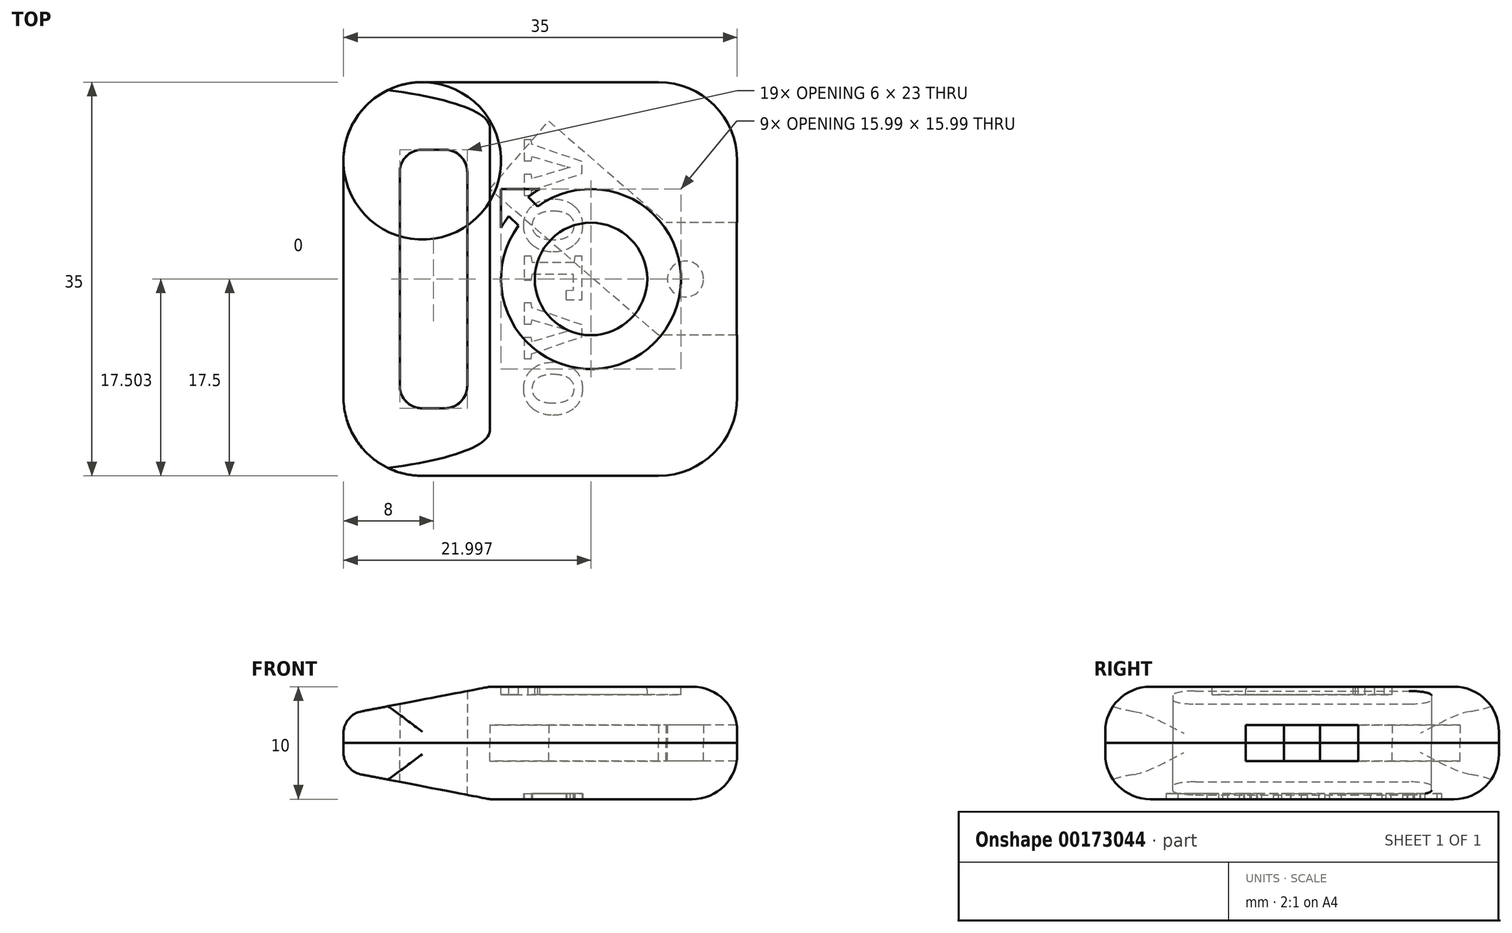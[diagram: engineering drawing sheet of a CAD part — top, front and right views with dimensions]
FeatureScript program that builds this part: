
annotation { "Feature Type Name" : "Feature", "Feature Type Description" : "" }
export const myFeature = defineFeature(function(context is Context, id is Id, definition is map)
    precondition{}
    {
        {
            var Q0;
            Q0=qCreatedBy(makeId("Top.planeOp"),FACE);
            var sketch = newSketch(context, id + "F0", { "sketchPlane" : qUnion([Q0])});
            skLineSegment(sketch, "E0.bottom", {"start": v(7, 0) * mm, "end": v(28, 0) * mm});
            skLineSegment(sketch, "E0.top", {"start": v(7, 35) * mm, "end": v(28, 35) * mm});
            skLineSegment(sketch, "E0.left", {"start": v(0, 7) * mm, "end": v(0, 28) * mm});
            skLineSegment(sketch, "E0.right", {"start": v(35, 7) * mm, "end": v(35, 28) * mm});
            skLineSegment(sketch, "E1.bottom", {"start": v(7, 29) * mm, "end": v(9, 29) * mm});
            skLineSegment(sketch, "E1.top", {"start": v(7, 6) * mm, "end": v(9, 6) * mm});
            skLineSegment(sketch, "E1.left", {"start": v(5, 27) * mm, "end": v(5, 8) * mm});
            skLineSegment(sketch, "E1.right", {"start": v(11, 27) * mm, "end": v(11, 8) * mm});
            skPoint(sketch, "E2.visualSharp", {"position": v(0, 35) * mm});
            skArc(sketch, "E2.filletArc", {"start": v(7, 35) * mm, "mid": v(2.05, 32.95) * mm, "end": v(0, 28) * mm});
            skPoint(sketch, "E3.visualSharp", {"position": v(35, 35) * mm});
            skArc(sketch, "E3.filletArc", {"start": v(35, 28) * mm, "mid": v(32.95, 32.95) * mm, "end": v(28, 35) * mm});
            skPoint(sketch, "E4.visualSharp", {"position": v(35, 0) * mm});
            skArc(sketch, "E4.filletArc", {"start": v(28, 0) * mm, "mid": v(32.95, 2.05) * mm, "end": v(35, 7) * mm});
            skPoint(sketch, "E5.visualSharp", {"position": v(0, 0) * mm});
            skArc(sketch, "E5.filletArc", {"start": v(0, 7) * mm, "mid": v(2.05, 2.05) * mm, "end": v(7, 0) * mm});
            skPoint(sketch, "E6.visualSharp", {"position": v(11, 29) * mm});
            skArc(sketch, "E6.filletArc", {"start": v(11, 27) * mm, "mid": v(10.41, 28.41) * mm, "end": v(9, 29) * mm});
            skPoint(sketch, "E7.visualSharp", {"position": v(11, 6) * mm});
            skArc(sketch, "E7.filletArc", {"start": v(9, 6) * mm, "mid": v(10.41, 6.59) * mm, "end": v(11, 8) * mm});
            skPoint(sketch, "E8.visualSharp", {"position": v(5, 29) * mm});
            skArc(sketch, "E8.filletArc", {"start": v(7, 29) * mm, "mid": v(5.59, 28.41) * mm, "end": v(5, 27) * mm});
            skPoint(sketch, "E9.visualSharp", {"position": v(5, 6) * mm});
            skArc(sketch, "E9.filletArc", {"start": v(5, 8) * mm, "mid": v(5.59, 6.59) * mm, "end": v(7, 6) * mm});
            skLineSegment(sketch, "E10.bottom", {"start": v(35, 12.5) * mm, "end": v(28, 12.5) * mm});
            skLineSegment(sketch, "E10.top", {"start": v(35, 22.5) * mm, "end": v(28, 22.5) * mm});
            skLineSegment(sketch, "E10.left", {"start": v(35, 12.5) * mm, "end": v(35, 22.5) * mm});
            skLineSegment(sketch, "E10.right", {"start": v(28, 12.5) * mm, "end": v(28, 22.5) * mm});
            skLineSegment(sketch, "E11", {"start": v(35, 17.5) * mm, "end": v(0, 17.5) * mm, "construction": true});
            skCircle(sketch, "E12", {"center": v(30.4, 17.5) * mm, "radius": 1.6 * mm});
            skLineSegment(sketch, "E13", {"start": v(28, 12.5) * mm, "end": v(13, 25.5) * mm});
            skLineSegment(sketch, "E14", {"start": v(13, 25.5) * mm, "end": v(18.24, 31.55) * mm});
            skLineSegment(sketch, "E15", {"start": v(18.24, 31.55) * mm, "end": v(28.68, 22.5) * mm});
            skSolve(sketch);
        }
        {
            var Q0;
            Q0=makeQuery(id+"F0.imprint","IMPRINT",FACE,{"disambiguationData":[TD([[makeQuery(id+"F0.imprint","IMPRINT",EDGE,{"derivedFrom":sQuery(id+"F0.wireOp",EDGE,"E0.bottom")}),1.0]])]});
            var Q1;
            {var subQ0=sQuery(id+"F0.wireOp",EDGE,"E10.right");Q1=makeQuery(id+"F0.imprint","IMPRINT",FACE,{"disambiguationData":[TD([[makeQuery(id+"F0.imprint","IMPRINT",EDGE,{"derivedFrom":subQ0}),1.0]])]});}
            var Q2;
            Q2=makeQuery(id+"F0.imprint","IMPRINT",FACE,{"disambiguationData":[TD([[makeQuery(id+"F0.imprint","IMPRINT",EDGE,{"derivedFrom":sQuery(id+"F0.wireOp",EDGE,"E10.bottom")}),-1.0]])]});
            var Q3;
            Q3=makeQuery(id+"F0.imprint","IMPRINT",FACE,{"disambiguationData":[TD([[makeQuery(id+"F0.imprint","IMPRINT",EDGE,{"derivedFrom":sQuery(id+"F0.wireOp",EDGE,"E12")}),1.0]])]});
            extrude(context, id + "F1", {"entities" : qUnion([Q0, Q1, Q2, Q3]), "oppositeDirection" : true, "depth" : 5 * mm});
        }
        {
            var Q0;
            {var subQ0=sQuery(id+"F0.wireOp",EDGE,"E10.right");Q0=makeQuery(id+"F0.imprint","IMPRINT",FACE,{"disambiguationData":[TD([[makeQuery(id+"F0.imprint","IMPRINT",EDGE,{"derivedFrom":subQ0}),1.0]])]});}
            var Q1;
            Q1=makeQuery(id+"F0.imprint","IMPRINT",FACE,{"disambiguationData":[TD([[makeQuery(id+"F0.imprint","IMPRINT",EDGE,{"derivedFrom":sQuery(id+"F0.wireOp",EDGE,"E10.bottom")}),-1.0]])]});
            extrude(context, id + "F2", {"entities" : qUnion([Q0, Q1]), "operationType" : NewBodyOperationType.REMOVE, "oppositeDirection" : true, "depth" : 1.6 * mm});
        }
        {
            var Q0;
            Q0=makeQuery(id+"F0.imprint","IMPRINT",FACE,{"disambiguationData":[TD([[makeQuery(id+"F0.imprint","IMPRINT",EDGE,{"derivedFrom":sQuery(id+"F0.wireOp",EDGE,"E0.bottom")}),1.0]])]});
            var Q1;
            {var subQ0=sQuery(id+"F0.wireOp",EDGE,"E10.right");Q1=makeQuery(id+"F0.imprint","IMPRINT",FACE,{"disambiguationData":[TD([[makeQuery(id+"F0.imprint","IMPRINT",EDGE,{"derivedFrom":subQ0}),1.0]])]});}
            var Q2;
            Q2=makeQuery(id+"F0.imprint","IMPRINT",FACE,{"disambiguationData":[TD([[makeQuery(id+"F0.imprint","IMPRINT",EDGE,{"derivedFrom":sQuery(id+"F0.wireOp",EDGE,"E10.bottom")}),-1.0]])]});
            var Q3;
            Q3=makeQuery(id+"F0.imprint","IMPRINT",FACE,{"disambiguationData":[TD([[makeQuery(id+"F0.imprint","IMPRINT",EDGE,{"derivedFrom":sQuery(id+"F0.wireOp",EDGE,"E12")}),1.0]])]});
            extrude(context, id + "F3", {"entities" : qUnion([Q0, Q1, Q2, Q3]), "depth" : 5 * mm});
        }
        {
            var Q0;
            {var subQ0=sQuery(id+"F0.wireOp",EDGE,"E10.right");Q0=makeQuery(id+"F0.imprint","IMPRINT",FACE,{"disambiguationData":[TD([[makeQuery(id+"F0.imprint","IMPRINT",EDGE,{"derivedFrom":subQ0}),1.0]])]});}
            var Q1;
            Q1=makeQuery(id+"F0.imprint","IMPRINT",FACE,{"disambiguationData":[TD([[makeQuery(id+"F0.imprint","IMPRINT",EDGE,{"derivedFrom":sQuery(id+"F0.wireOp",EDGE,"E10.bottom")}),-1.0]])]});
            extrude(context, id + "F4", {"entities" : qUnion([Q0, Q1]), "operationType" : NewBodyOperationType.REMOVE, "depth" : 1.6 * mm});
        }
        {
            var Q0;
            Q0=makeQuery(id+"F3.opExtrude","CAP_EDGE",EDGE,{"disambiguationData":[OSD([sQuery(id+"F0.wireOp",EDGE,"E0.left")])],"isStart":false});
            chamfer(context, id + "F5", {"entities" : qUnion([Q0]), "chamferType" : ChamferType.TWO_OFFSETS, "width1" : 2.5 * mm, "oppositeDirection" : false, "width2" : 13 * mm});
        }
        {
            var Q0;
            Q0=makeQuery(id+"F1.opExtrude","CAP_EDGE",EDGE,{"disambiguationData":[OSD([sQuery(id+"F0.wireOp",EDGE,"E0.left")])],"isStart":false});
            chamfer(context, id + "F6", {"entities" : qUnion([Q0]), "chamferType" : ChamferType.TWO_OFFSETS, "width1" : 13 * mm, "oppositeDirection" : false, "width2" : 2.5 * mm});
        }
        {
            var Q0;
            Q0=makeQuery(id+"F3.opExtrude","CAP_EDGE",EDGE,{"disambiguationData":[OSD([sQuery(id+"F0.wireOp",EDGE,"E0.bottom")])],"isStart":false});
            var Q1;
            Q1=makeQuery(id+"F1.opExtrude","CAP_EDGE",EDGE,{"disambiguationData":[OSD([sQuery(id+"F0.wireOp",EDGE,"E0.right"),sQuery(id+"F0.wireOp",EDGE,"E10.left")])],"isStart":false});
            fillet(context, id + "F7", {"entities" : qUnion([Q0, Q1]), "radius" : 4 * mm, "tangentPropagation" : true, "allowEdgeOverflow" : false});
        }
        {
            var Q0;
            {var subQ0=sQuery(id+"F0.wireOp",EDGE,"E0.left");Q0=makeQuery(id+"F5.opChamfer","BLEND_EDGE",EDGE,{"blendedFrom":[makeQuery(id+"F3.opExtrude","CAP_EDGE",EDGE,{"disambiguationData":[OSD([subQ0])],"isStart":false}),makeQuery(id+"F3.opExtrude","SWEPT_FACE",FACE,{"disambiguationData":[OSD([subQ0])]})],"blendedInto":[makeQuery(id+"F3.opExtrude","SWEPT_FACE",FACE,{"disambiguationData":[OSD([subQ0])]})]});}
            var Q1;
            {var subQ0=sQuery(id+"F0.wireOp",EDGE,"E0.left");Q1=makeQuery(id+"F6.opChamfer","BLEND_EDGE",EDGE,{"blendedFrom":[makeQuery(id+"F1.opExtrude","CAP_EDGE",EDGE,{"disambiguationData":[OSD([subQ0])],"isStart":false}),makeQuery(id+"F1.opExtrude","SWEPT_FACE",FACE,{"disambiguationData":[OSD([subQ0])]})],"blendedInto":[makeQuery(id+"F1.opExtrude","SWEPT_FACE",FACE,{"disambiguationData":[OSD([subQ0])]})]});}
            fillet(context, id + "F8", {"entities" : qUnion([Q0, Q1]), "radius" : 2 * mm, "allowEdgeOverflow" : false});
        }
        {
            var Q0;
            Q0=makeQuery(id+"F3.opExtrude","CAP_FACE",FACE,{"disambiguationData":[OSD([sQuery(id+"F0.wireOp",EDGE,"E0.bottom"),sQuery(id+"F0.wireOp",EDGE,"E0.top"),sQuery(id+"F0.wireOp",EDGE,"E0.left"),sQuery(id+"F0.wireOp",EDGE,"E0.right"),sQuery(id+"F0.wireOp",EDGE,"E1.bottom"),sQuery(id+"F0.wireOp",EDGE,"E1.top"),sQuery(id+"F0.wireOp",EDGE,"E1.left"),sQuery(id+"F0.wireOp",EDGE,"E1.right"),sQuery(id+"F0.wireOp",EDGE,"E2.filletArc"),sQuery(id+"F0.wireOp",EDGE,"E3.filletArc"),sQuery(id+"F0.wireOp",EDGE,"E4.filletArc"),sQuery(id+"F0.wireOp",EDGE,"E5.filletArc"),sQuery(id+"F0.wireOp",EDGE,"E6.filletArc"),sQuery(id+"F0.wireOp",EDGE,"E7.filletArc"),sQuery(id+"F0.wireOp",EDGE,"E8.filletArc"),sQuery(id+"F0.wireOp",EDGE,"E9.filletArc"),sQuery(id+"F0.wireOp",EDGE,"E10.left")])],"isStart":false});
            var sketch = newSketch(context, id + "F9", { "sketchPlane" : qUnion([Q0])});
            skCircle(sketch, "E16", {"center": v(22, 17.5) * mm, "radius": 5 * mm});
            skCircle(sketch, "E17", {"center": v(22, 17.5) * mm, "radius": 8 * mm});
            skLineSegment(sketch, "E18", {"start": v(11.27, 25.5) * mm, "end": v(37.16, 25.5) * mm, "construction": true});
            skLineSegment(sketch, "E19", {"start": v(30, 5.1) * mm, "end": v(30, 29) * mm, "construction": true});
            skLineSegment(sketch, "E20", {"start": v(30, 25.5) * mm, "end": v(26.54, 25.5) * mm});
            skLineSegment(sketch, "E21", {"start": v(22, 17.5) * mm, "end": v(32.02, 27.52) * mm, "construction": true});
            skLineSegment(sketch, "E22", {"start": v(27.6, 24.8) * mm, "end": v(24.58, 21.78) * mm});
            skArc(sketch, "E23", {"start": v(27.6, 24.8) * mm, "mid": v(27.08, 25.17) * mm, "end": v(26.54, 25.5) * mm});
            skLineSegment(sketch, "E24.MirrorCS", {"start": v(30, 25.5) * mm, "end": v(30, 22.04) * mm});
            skArc(sketch, "E25.MirrorCS", {"start": v(29.3, 23.1) * mm, "mid": v(29.67, 22.58) * mm, "end": v(30, 22.04) * mm});
            skLineSegment(sketch, "E26.MirrorCS", {"start": v(29.3, 23.1) * mm, "end": v(26.28, 20.08) * mm});
            skLineSegment(sketch, "E27", {"start": v(31, 17.5) * mm, "end": v(13, 17.5) * mm, "construction": true});
            skLineSegment(sketch, "E28.MirrorCS", {"start": v(30, 9.5) * mm, "end": v(26.54, 9.5) * mm});
            skArc(sketch, "E29.MirrorCS", {"start": v(27.6, 10.2) * mm, "mid": v(27.08, 9.83) * mm, "end": v(26.54, 9.5) * mm});
            skLineSegment(sketch, "E30.MirrorCS", {"start": v(27.6, 10.2) * mm, "end": v(24.58, 13.22) * mm});
            skLineSegment(sketch, "E31.MirrorCS", {"start": v(29.3, 11.9) * mm, "end": v(26.28, 14.92) * mm});
            skLineSegment(sketch, "E32.MirrorCS", {"start": v(30, 9.5) * mm, "end": v(30, 12.96) * mm});
            skArc(sketch, "E33.MirrorCS", {"start": v(29.3, 11.9) * mm, "mid": v(29.67, 12.42) * mm, "end": v(30, 12.96) * mm});
            skLineSegment(sketch, "E34", {"start": v(22, 5.05) * mm, "end": v(22, 27.17) * mm, "construction": true});
            skLineSegment(sketch, "E35.MirrorCS", {"start": v(16.4, 10.2) * mm, "end": v(19.42, 13.22) * mm});
            skLineSegment(sketch, "E36.MirrorCS", {"start": v(14.7, 11.9) * mm, "end": v(17.72, 14.92) * mm});
            skArc(sketch, "E37.MirrorCS", {"start": v(16.4, 10.2) * mm, "mid": v(16.92, 9.83) * mm, "end": v(17.46, 9.5) * mm});
            skLineSegment(sketch, "E38.MirrorCS", {"start": v(14, 9.5) * mm, "end": v(14, 12.96) * mm});
            skLineSegment(sketch, "E39.MirrorCS", {"start": v(14, 9.5) * mm, "end": v(17.46, 9.5) * mm});
            skArc(sketch, "E40.MirrorCS", {"start": v(14.7, 11.9) * mm, "mid": v(14.33, 12.42) * mm, "end": v(14, 12.96) * mm});
            skArc(sketch, "E41.MirrorCS", {"start": v(14.7, 23.1) * mm, "mid": v(14.33, 22.58) * mm, "end": v(14, 22.04) * mm});
            skLineSegment(sketch, "E42.MirrorCS", {"start": v(16.4, 24.8) * mm, "end": v(19.42, 21.78) * mm});
            skLineSegment(sketch, "E43.MirrorCS", {"start": v(14, 25.5) * mm, "end": v(17.46, 25.5) * mm});
            skArc(sketch, "E44.MirrorCS", {"start": v(16.4, 24.8) * mm, "mid": v(16.92, 25.17) * mm, "end": v(17.46, 25.5) * mm});
            skLineSegment(sketch, "E45.MirrorCS", {"start": v(14.7, 23.1) * mm, "end": v(17.72, 20.08) * mm});
            skLineSegment(sketch, "E46.MirrorCS", {"start": v(14, 25.5) * mm, "end": v(14, 22.04) * mm});
            skSolve(sketch);
        }
        {
            var Q0;
            {var subQ0=sQuery(id+"F9.wireOp",EDGE,"E22");var subQ1=sQuery(id+"F9.wireOp",EDGE,"E16");var subQ2=makeQuery(id+"F9.imprint","INTERSECT",VERTEX,{"derivedFrom":[subQ1,subQ0]});Q0=makeQuery(id+"F9.imprint","IMPRINT",FACE,{"disambiguationData":[TD([[makeQuery(id+"F9.imprint","IMPRINT",EDGE,{"disambiguationData":[TD([[subQ2,1.0]])],"derivedFrom":subQ1}),-1.0]])]});}
            var Q1;
            {var subQ0=sQuery(id+"F9.wireOp",EDGE,"E22");var subQ1=sQuery(id+"F9.wireOp",EDGE,"E16");var subQ2=makeQuery(id+"F9.imprint","INTERSECT",VERTEX,{"derivedFrom":[subQ1,subQ0]});Q1=makeQuery(id+"F9.imprint","IMPRINT",FACE,{"disambiguationData":[TD([[makeQuery(id+"F9.imprint","IMPRINT",EDGE,{"disambiguationData":[TD([[subQ2,-1.0]])],"derivedFrom":subQ1}),-1.0]])]});}
            var Q2;
            {var subQ0=sQuery(id+"F9.wireOp",EDGE,"E26.MirrorCS");var subQ1=sQuery(id+"F9.wireOp",EDGE,"E16");var subQ2=makeQuery(id+"F9.imprint","INTERSECT",VERTEX,{"derivedFrom":[subQ1,subQ0]});Q2=makeQuery(id+"F9.imprint","IMPRINT",FACE,{"disambiguationData":[TD([[makeQuery(id+"F9.imprint","IMPRINT",EDGE,{"disambiguationData":[TD([[subQ2,1.0]])],"derivedFrom":subQ1}),-1.0]])]});}
            var Q3;
            {var subQ0=sQuery(id+"F9.wireOp",EDGE,"E30.MirrorCS");var subQ1=sQuery(id+"F9.wireOp",EDGE,"E16");var subQ2=makeQuery(id+"F9.imprint","INTERSECT",VERTEX,{"derivedFrom":[subQ1,subQ0]});Q3=makeQuery(id+"F9.imprint","IMPRINT",FACE,{"disambiguationData":[TD([[makeQuery(id+"F9.imprint","IMPRINT",EDGE,{"disambiguationData":[TD([[subQ2,-1.0]])],"derivedFrom":subQ1}),-1.0]])]});}
            var Q4;
            {var subQ0=sQuery(id+"F9.wireOp",EDGE,"E30.MirrorCS");var subQ1=sQuery(id+"F9.wireOp",EDGE,"E16");var subQ2=makeQuery(id+"F9.imprint","INTERSECT",VERTEX,{"derivedFrom":[subQ1,subQ0]});Q4=makeQuery(id+"F9.imprint","IMPRINT",FACE,{"disambiguationData":[TD([[makeQuery(id+"F9.imprint","IMPRINT",EDGE,{"disambiguationData":[TD([[subQ2,1.0]])],"derivedFrom":subQ1}),-1.0]])]});}
            var Q5;
            {var subQ0=sQuery(id+"F9.wireOp",EDGE,"E35.MirrorCS");var subQ1=sQuery(id+"F9.wireOp",EDGE,"E16");var subQ2=makeQuery(id+"F9.imprint","INTERSECT",VERTEX,{"derivedFrom":[subQ1,subQ0]});Q5=makeQuery(id+"F9.imprint","IMPRINT",FACE,{"disambiguationData":[TD([[makeQuery(id+"F9.imprint","IMPRINT",EDGE,{"disambiguationData":[TD([[subQ2,1.0]])],"derivedFrom":subQ1}),-1.0]])]});}
            var Q6;
            {var subQ0=sQuery(id+"F9.wireOp",EDGE,"E36.MirrorCS");var subQ1=sQuery(id+"F9.wireOp",EDGE,"E16");var subQ2=makeQuery(id+"F9.imprint","INTERSECT",VERTEX,{"derivedFrom":[subQ1,subQ0]});Q6=makeQuery(id+"F9.imprint","IMPRINT",FACE,{"disambiguationData":[TD([[makeQuery(id+"F9.imprint","IMPRINT",EDGE,{"disambiguationData":[TD([[subQ2,1.0]])],"derivedFrom":subQ1}),-1.0]])]});}
            var Q7;
            {var subQ0=sQuery(id+"F9.wireOp",EDGE,"E42.MirrorCS");var subQ1=sQuery(id+"F9.wireOp",EDGE,"E16");var subQ2=makeQuery(id+"F9.imprint","INTERSECT",VERTEX,{"derivedFrom":[subQ1,subQ0]});Q7=makeQuery(id+"F9.imprint","IMPRINT",FACE,{"disambiguationData":[TD([[makeQuery(id+"F9.imprint","IMPRINT",EDGE,{"disambiguationData":[TD([[subQ2,-1.0]])],"derivedFrom":subQ1}),-1.0]])]});}
            var Q8;
            {var subQ4=sQuery(id+"F9.wireOp",EDGE,"E41.MirrorCS");Q8=makeQuery(id+"F9.imprint","IMPRINT",FACE,{"disambiguationData":[TD([[makeQuery(id+"F9.imprint","IMPRINT",EDGE,{"derivedFrom":subQ4}),-1.0]])]});}
            extrude(context, id + "F10", {"entities" : qUnion([Q0, Q1, Q2, Q3, Q4, Q5, Q6, Q7, Q8]), "operationType" : NewBodyOperationType.REMOVE, "oppositeDirection" : true, "depth" : 0.7 * mm});
        }
        {
            var Q0;
            Q0=makeQuery(id+"F10.boolean.opBoolean","COPY",EDGE,{"derivedFrom":makeQuery(id+"F10.opExtrude","CAP_EDGE",EDGE,{"disambiguationData":[OSD([sQuery(id+"F9.wireOp",EDGE,"E17")])],"isStart":true})});
            var Q1;
            Q1=makeQuery(id+"F10.boolean.opBoolean","COPY",EDGE,{"derivedFrom":makeQuery(id+"F10.opExtrude","CAP_EDGE",EDGE,{"disambiguationData":[OSD([sQuery(id+"F9.wireOp",EDGE,"E16")])],"isStart":true})});
            var Q2;
            Q2=makeQuery(id+"F10.boolean.opBoolean","COPY",EDGE,{"derivedFrom":makeQuery(id+"F10.opExtrude","CAP_EDGE",EDGE,{"disambiguationData":[OSD([sQuery(id+"F9.wireOp",EDGE,"E32.MirrorCS")])],"isStart":true})});
            var Q3;
            Q3=makeQuery(id+"F10.boolean.opBoolean","COPY",EDGE,{"derivedFrom":makeQuery(id+"F10.opExtrude","CAP_EDGE",EDGE,{"disambiguationData":[OSD([sQuery(id+"F9.wireOp",EDGE,"E28.MirrorCS")])],"isStart":true})});
            var Q4;
            Q4=makeQuery(id+"F10.boolean.opBoolean","COPY",EDGE,{"derivedFrom":makeQuery(id+"F10.opExtrude","CAP_EDGE",EDGE,{"disambiguationData":[OSD([sQuery(id+"F9.wireOp",EDGE,"E33.MirrorCS")])],"isStart":true})});
            var Q5;
            Q5=makeQuery(id+"F10.boolean.opBoolean","COPY",EDGE,{"derivedFrom":makeQuery(id+"F10.opExtrude","CAP_EDGE",EDGE,{"disambiguationData":[OSD([sQuery(id+"F9.wireOp",EDGE,"E29.MirrorCS")])],"isStart":true})});
            var Q6;
            Q6=makeQuery(id+"F10.boolean.opBoolean","COPY",EDGE,{"derivedFrom":makeQuery(id+"F10.opExtrude","CAP_EDGE",EDGE,{"disambiguationData":[OSD([sQuery(id+"F9.wireOp",EDGE,"E30.MirrorCS")])],"isStart":true})});
            var Q7;
            Q7=makeQuery(id+"F10.boolean.opBoolean","COPY",EDGE,{"derivedFrom":makeQuery(id+"F10.opExtrude","CAP_EDGE",EDGE,{"disambiguationData":[OSD([sQuery(id+"F9.wireOp",EDGE,"E31.MirrorCS")])],"isStart":true})});
            fillet(context, id + "F11", {"entities" : qUnion([Q0, Q1, Q2, Q3, Q4, Q5, Q6, Q7]), "radius" : 0.3 * mm, "tangentPropagation" : true, "allowEdgeOverflow" : false});
        }
        {
            var Q0;
            Q0=makeQuery(id+"F1.opExtrude","CAP_FACE",FACE,{"disambiguationData":[OSD([sQuery(id+"F0.wireOp",EDGE,"E0.bottom"),sQuery(id+"F0.wireOp",EDGE,"E0.top"),sQuery(id+"F0.wireOp",EDGE,"E0.left"),sQuery(id+"F0.wireOp",EDGE,"E0.right"),sQuery(id+"F0.wireOp",EDGE,"E1.bottom"),sQuery(id+"F0.wireOp",EDGE,"E1.top"),sQuery(id+"F0.wireOp",EDGE,"E1.left"),sQuery(id+"F0.wireOp",EDGE,"E1.right"),sQuery(id+"F0.wireOp",EDGE,"E2.filletArc"),sQuery(id+"F0.wireOp",EDGE,"E3.filletArc"),sQuery(id+"F0.wireOp",EDGE,"E4.filletArc"),sQuery(id+"F0.wireOp",EDGE,"E5.filletArc"),sQuery(id+"F0.wireOp",EDGE,"E6.filletArc"),sQuery(id+"F0.wireOp",EDGE,"E7.filletArc"),sQuery(id+"F0.wireOp",EDGE,"E8.filletArc"),sQuery(id+"F0.wireOp",EDGE,"E9.filletArc"),sQuery(id+"F0.wireOp",EDGE,"E10.left")])],"isStart":false});
            var sketch = newSketch(context, id + "F12", { "sketchPlane" : qUnion([Q0])});
            skText(sketch, "E47", { "text": "VOLVO", "fontName": "RobotoSlab-Bold.ttf"});
            const initialGuessF12  = {"E47": [0.0212, -0.03, 0, 1, 0.0052]};
            skSetInitialGuess(sketch, initialGuessF12);
            skSolve(sketch);
        }
        {
            var Q0;
            Q0 = qSketchRegion(id + "F12", true);
            extrude(context, id + "F13", {"entities" : qUnion([Q0]), "operationType" : NewBodyOperationType.REMOVE, "oppositeDirection" : true, "depth" : 0.5 * mm});
        }
    });
